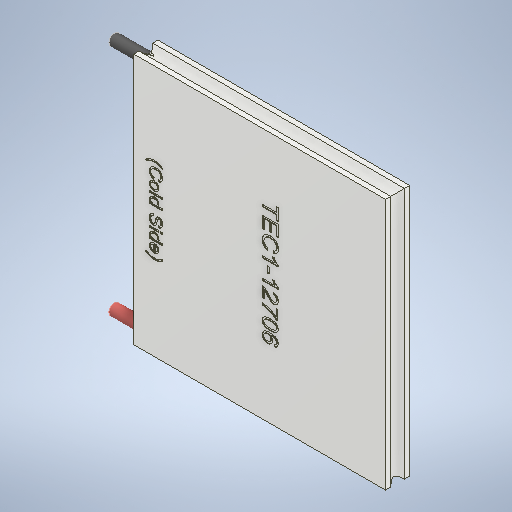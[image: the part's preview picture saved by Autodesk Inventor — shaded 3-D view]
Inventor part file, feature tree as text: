
AUTODESK INVENTOR PART (.ipt)
format: ipt  version: 2025.2 (Build 292293000, 293)  size: 893,440 bytes
history: native  units: in
note: dims shown in document units (in); Inventor stores cm internally (conversion verified against a paired STEP export)
features: other x3, plane x2
ambient origin geometry x8: Origin, YZ Plane, XZ Plane, XY Plane, X Axis, Y Axis, Z Axis, Center Point
bodies: Solid1 (feature_tree), Solid2 (feature_tree), Solid3 (feature_tree)
feature tree (5):
  plane  "Work Plane1"
  plane  "Work Plane2"
  other  "Positive"
  other  "Negative"
  other  "TEC Module"
